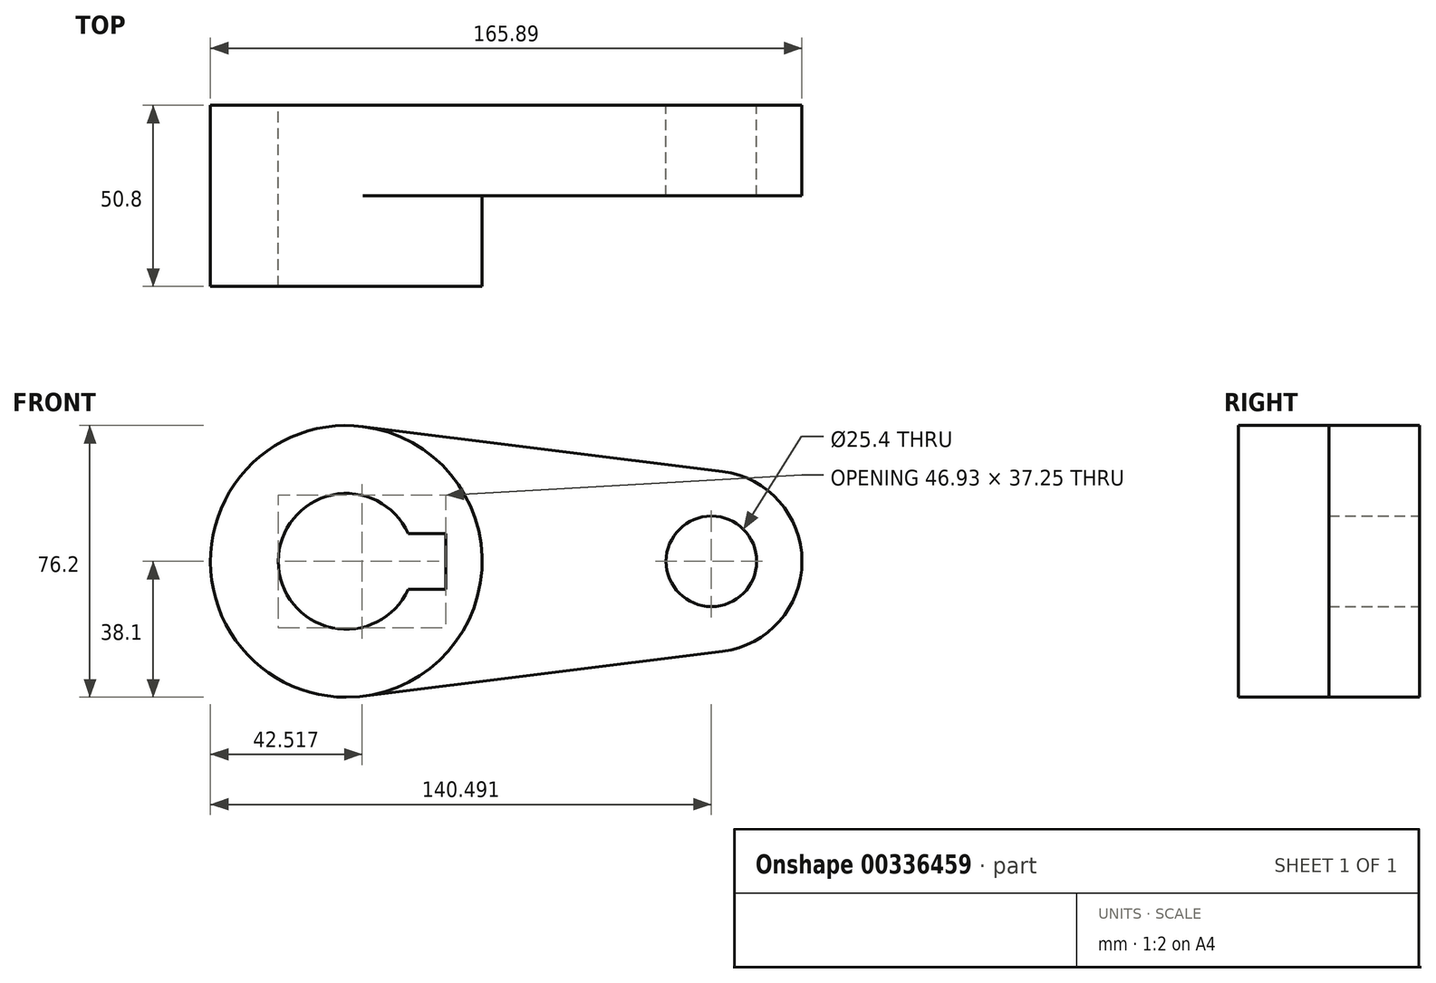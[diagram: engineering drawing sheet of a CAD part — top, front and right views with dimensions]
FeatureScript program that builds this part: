
annotation { "Feature Type Name" : "Feature", "Feature Type Description" : "" }
export const myFeature = defineFeature(function(context is Context, id is Id, definition is map)
    precondition{}
    {
        {
            var Q0;
            Q0=qCreatedBy(makeId("Front.planeOp"),FACE);
            var sketch = newSketch(context, id + "F0", { "sketchPlane" : qUnion([Q0])});
            skCircle(sketch, "E0", {"center": v(0, 0) * mm, "radius": 38.1 * mm});
            skCircle(sketch, "E1", {"center": v(102.4, 0) * mm, "radius": 25.4 * mm});
            skLineSegment(sketch, "E2", {"start": v(4.73, 37.8) * mm, "end": v(105.54, 25.2) * mm});
            skLineSegment(sketch, "E3", {"start": v(4.73, -37.8) * mm, "end": v(105.54, -25.2) * mm});
            skCircle(sketch, "E4", {"center": v(0, 0) * mm, "radius": 19.05 * mm});
            skCircle(sketch, "E5", {"center": v(102.4, 0) * mm, "radius": 12.7 * mm});
            skLineSegment(sketch, "E6.bottom", {"start": v(-22.92, 7.83) * mm, "end": v(27.88, 7.83) * mm});
            skLineSegment(sketch, "E6.top", {"start": v(-22.92, -7.83) * mm, "end": v(27.88, -7.83) * mm});
            skLineSegment(sketch, "E6.right", {"start": v(27.88, 7.83) * mm, "end": v(27.88, -7.83) * mm});
            skLineSegment(sketch, "E7", {"start": v(-22.92, 0) * mm, "end": v(-22.92, -7.83) * mm});
            skLineSegment(sketch, "E8", {"start": v(-22.92, 0) * mm, "end": v(-22.92, 7.83) * mm});
            skSolve(sketch);
        }
        {
            var Q0;
            {var subQ7=sQuery(id+"F0.wireOp",EDGE,"E6.left");Q0=makeQuery(id+"F0.imprint","IMPRINT",FACE,{"disambiguationData":[TD([[makeQuery(id+"F0.imprint","IMPRINT",EDGE,{"derivedFrom":subQ7}),-1.0]])]});}
            var Q1;
            {var subQ0=sQuery(id+"F0.wireOp",EDGE,"E2");Q1=makeQuery(id+"F0.imprint","IMPRINT",FACE,{"disambiguationData":[TD([[makeQuery(id+"F0.imprint","IMPRINT",EDGE,{"derivedFrom":subQ0}),-1.0]])]});}
            var Q2;
            Q2=makeQuery(id+"F0.imprint","IMPRINT",FACE,{"disambiguationData":[TD([[makeQuery(id+"F0.imprint","IMPRINT",EDGE,{"derivedFrom":sQuery(id+"F0.wireOp",EDGE,"E5")}),-1.0]])]});
            var Q3;
            {var subQ5=sQuery(id+"F0.wireOp",EDGE,"E6.left");Q3=makeQuery(id+"F0.imprint","IMPRINT",FACE,{"disambiguationData":[TD([[makeQuery(id+"F0.imprint","IMPRINT",EDGE,{"derivedFrom":subQ5}),1.0]])]});}
            var Q4;
            {var subQ1=sQuery(id+"F0.wireOp",EDGE,"E6.right");Q4=makeQuery(id+"F0.imprint","IMPRINT",FACE,{"disambiguationData":[TD([[makeQuery(id+"F0.imprint","IMPRINT",EDGE,{"derivedFrom":subQ1}),1.0]])]});}
            var Q5;
            {var subQ0=sQuery(id+"F0.wireOp",EDGE,"E7");Q5=makeQuery(id+"F0.imprint","IMPRINT",FACE,{"disambiguationData":[TD([[makeQuery(id+"F0.imprint","IMPRINT",EDGE,{"derivedFrom":subQ0}),1.0]])]});}
            extrude(context, id + "F1", {"entities" : qUnion([Q0, Q1, Q2, Q3, Q4, Q5]), "depth" : 25.4 * mm});
        }
        {
            var Q0;
            {var subQ7=sQuery(id+"F0.wireOp",EDGE,"E6.left");Q0=makeQuery(id+"F0.imprint","IMPRINT",FACE,{"disambiguationData":[TD([[makeQuery(id+"F0.imprint","IMPRINT",EDGE,{"derivedFrom":subQ7}),-1.0]])]});}
            var Q1;
            {var subQ5=sQuery(id+"F0.wireOp",EDGE,"E6.left");Q1=makeQuery(id+"F0.imprint","IMPRINT",FACE,{"disambiguationData":[TD([[makeQuery(id+"F0.imprint","IMPRINT",EDGE,{"derivedFrom":subQ5}),1.0]])]});}
            var Q2;
            {var subQ1=sQuery(id+"F0.wireOp",EDGE,"E6.right");Q2=makeQuery(id+"F0.imprint","IMPRINT",FACE,{"disambiguationData":[TD([[makeQuery(id+"F0.imprint","IMPRINT",EDGE,{"derivedFrom":subQ1}),1.0]])]});}
            var Q3;
            {var subQ0=sQuery(id+"F0.wireOp",EDGE,"E7");Q3=makeQuery(id+"F0.imprint","IMPRINT",FACE,{"disambiguationData":[TD([[makeQuery(id+"F0.imprint","IMPRINT",EDGE,{"derivedFrom":subQ0}),1.0]])]});}
            extrude(context, id + "F2", {"entities" : qUnion([Q0, Q1, Q2, Q3]), "operationType" : NewBodyOperationType.ADD, "depth" : 50.8 * mm});
        }
    });
